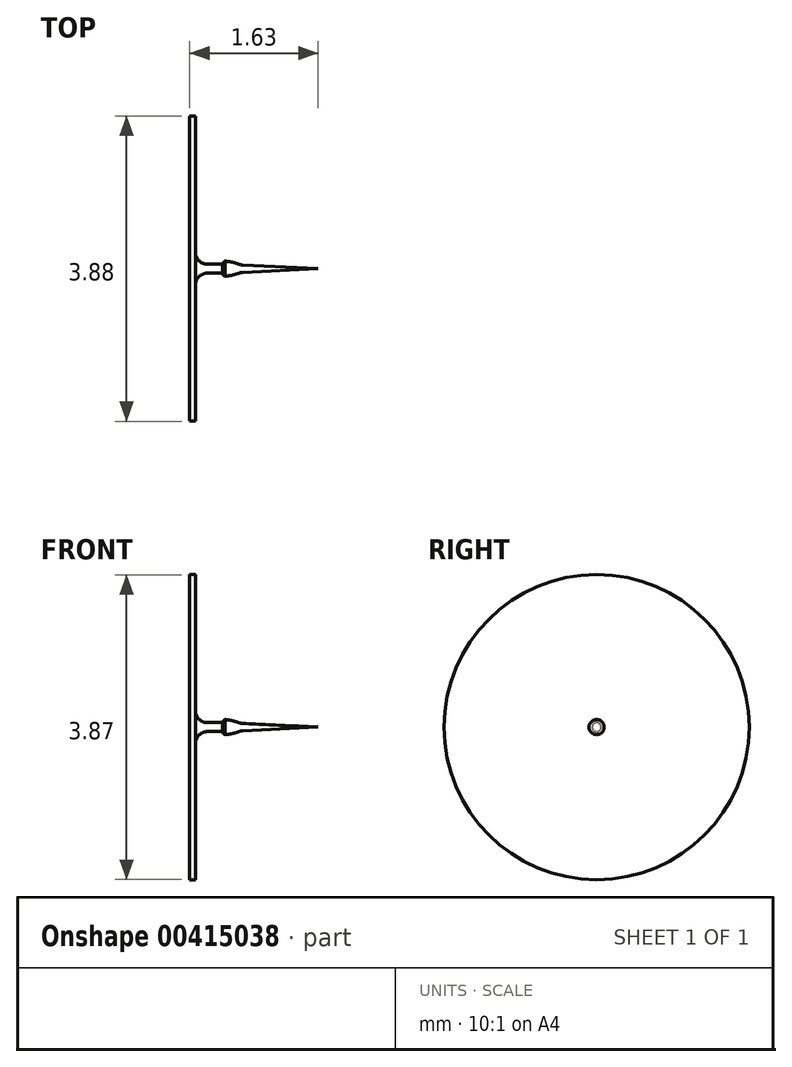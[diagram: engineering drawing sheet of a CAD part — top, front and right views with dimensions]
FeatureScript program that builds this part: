
annotation { "Feature Type Name" : "Feature", "Feature Type Description" : "" }
export const myFeature = defineFeature(function(context is Context, id is Id, definition is map)
    precondition{}
    {
        {
            var Q0;
            Q0=qCreatedBy(makeId("Front.planeOp"),FACE);
            var sketch = newSketch(context, id + "F0", { "sketchPlane" : qUnion([Q0])});
            skLineSegment(sketch, "E0.bottom", {"start": v(-10.35, 1.78) * mm, "end": v(14.65, 1.78) * mm});
            skLineSegment(sketch, "E0.top", {"start": v(-10.35, 0.78) * mm, "end": v(14.65, 0.78) * mm});
            skLineSegment(sketch, "E0.left", {"start": v(-10.35, 1.78) * mm, "end": v(-10.35, 0.78) * mm});
            skLineSegment(sketch, "E0.right", {"start": v(14.65, 1.78) * mm, "end": v(14.65, 0.78) * mm});
            skLineSegment(sketch, "E1", {"start": v(-10.35, -1.22) * mm, "end": v(14.65, -1.22) * mm});
            skLineSegment(sketch, "E2.bottom", {"start": v(8.36, 0.78) * mm, "end": v(8.11, 0.78) * mm});
            skLineSegment(sketch, "E2.top", {"start": v(8.36, 0.43) * mm, "end": v(8.11, 0.43) * mm});
            skLineSegment(sketch, "E2.left", {"start": v(8.36, 0.78) * mm, "end": v(8.36, 0.43) * mm});
            skLineSegment(sketch, "E2.right", {"start": v(8.11, 0.78) * mm, "end": v(8.11, 0.43) * mm});
            skArc(sketch, "E3", {"start": v(-10.35, 0.78) * mm, "mid": v(-9.78, 0.5) * mm, "end": v(-9.2, 0.78) * mm});
            skArc(sketch, "E4", {"start": v(5.04, 1.78) * mm, "mid": v(2.54, 2.32) * mm, "end": v(0.04, 1.78) * mm});
            skLineSegment(sketch, "E5.bottom", {"start": v(5.04, 0.71) * mm, "end": v(8.06, 0.71) * mm});
            skLineSegment(sketch, "E5.top", {"start": v(5.04, -0.04) * mm, "end": v(8.06, -0.04) * mm});
            skLineSegment(sketch, "E5.left", {"start": v(5.04, 0.71) * mm, "end": v(5.04, -0.04) * mm});
            skLineSegment(sketch, "E5.right", {"start": v(8.06, 0.71) * mm, "end": v(8.06, -0.06) * mm});
            skLineSegment(sketch, "E6.bottom", {"start": v(8.06, 0.35) * mm, "end": v(8.72, 0.35) * mm});
            skLineSegment(sketch, "E6.top", {"start": v(8.06, -1.22) * mm, "end": v(8.72, -1.22) * mm});
            skLineSegment(sketch, "E6.left", {"start": v(8.06, 0.35) * mm, "end": v(8.06, -1.22) * mm});
            skLineSegment(sketch, "E6.right", {"start": v(8.72, 0.35) * mm, "end": v(8.72, -1.22) * mm});
            skLineSegment(sketch, "E7.bottom", {"start": v(7.8, -0.04) * mm, "end": v(8.06, -0.04) * mm});
            skLineSegment(sketch, "E7.top", {"start": v(7.8, -1.22) * mm, "end": v(8.06, -1.22) * mm});
            skLineSegment(sketch, "E7.left", {"start": v(7.8, -0.04) * mm, "end": v(7.8, -1.22) * mm});
            skLineSegment(sketch, "E7.right", {"start": v(8.06, -0.04) * mm, "end": v(8.06, -1.22) * mm});
            skLineSegment(sketch, "E8.bottom", {"start": v(-3.72, 0.71) * mm, "end": v(-8.72, 0.71) * mm});
            skLineSegment(sketch, "E8.top", {"start": v(-3.72, -0.04) * mm, "end": v(-8.72, -0.04) * mm});
            skLineSegment(sketch, "E8.left", {"start": v(-3.72, 0.71) * mm, "end": v(-3.72, -0.04) * mm});
            skLineSegment(sketch, "E8.right", {"start": v(-8.72, 0.71) * mm, "end": v(-8.72, -0.04) * mm});
            skLineSegment(sketch, "E9.bottom", {"start": v(-8.72, -0.04) * mm, "end": v(-8.47, -0.04) * mm});
            skLineSegment(sketch, "E9.top", {"start": v(-8.72, -0.29) * mm, "end": v(-8.47, -0.29) * mm});
            skLineSegment(sketch, "E9.left", {"start": v(-8.72, -0.04) * mm, "end": v(-8.72, -0.29) * mm});
            skLineSegment(sketch, "E9.right", {"start": v(-8.47, -0.04) * mm, "end": v(-8.47, -0.29) * mm});
            skLineSegment(sketch, "E10.bottom", {"start": v(-8.72, -1.14) * mm, "end": v(-8.47, -1.14) * mm});
            skLineSegment(sketch, "E10.top", {"start": v(-8.72, -0.99) * mm, "end": v(-8.47, -0.99) * mm});
            skLineSegment(sketch, "E10.left", {"start": v(-8.72, -1.14) * mm, "end": v(-8.72, -0.99) * mm});
            skLineSegment(sketch, "E10.right", {"start": v(-8.47, -1.14) * mm, "end": v(-8.47, -0.99) * mm});
            skLineSegment(sketch, "E11.left", {"start": v(-8.72, -0.29) * mm, "end": v(-8.72, -0.99) * mm});
            skLineSegment(sketch, "E11.right", {"start": v(-8.47, -0.29) * mm, "end": v(-8.47, -0.99) * mm});
            skLineSegment(sketch, "E12", {"start": v(-8.86, -1.22) * mm, "end": v(-8.86, 0.71) * mm});
            skLineSegment(sketch, "E13", {"start": v(-8.86, 0.71) * mm, "end": v(-8.79, 0.71) * mm});
            skLineSegment(sketch, "E14", {"start": v(-8.79, 0.71) * mm, "end": v(-8.79, -1.17) * mm});
            skLineSegment(sketch, "E15", {"start": v(-8.79, -1.17) * mm, "end": v(-8.38, -1.17) * mm});
            skLineSegment(sketch, "E16", {"start": v(-8.38, -1.17) * mm, "end": v(-7.23, -1.22) * mm});
            skArc(sketch, "E17", {"start": v(-8.4, -1.13) * mm, "mid": v(-8.43, -1.14) * mm, "end": v(-8.44, -1.17) * mm});
            skArc(sketch, "E18", {"start": v(-8.21, -1.18) * mm, "mid": v(-8.3, -1.14) * mm, "end": v(-8.4, -1.13) * mm});
            skSolve(sketch);
        }
        {
            var Q0;
            {var subQ0=sQuery(id+"F0.wireOp",EDGE,"E12");Q0=makeQuery(id+"F0.imprint","IMPRINT",FACE,{"disambiguationData":[TD([[makeQuery(id+"F0.imprint","IMPRINT",EDGE,{"derivedFrom":subQ0}),-1.0]])]});}
            var Q1;
            {var subQ3=sQuery(id+"F0.wireOp",EDGE,"E17");Q1=makeQuery(id+"F0.imprint","IMPRINT",FACE,{"disambiguationData":[TD([[makeQuery(id+"F0.imprint","IMPRINT",EDGE,{"derivedFrom":subQ3}),1.0]])]});}
            var Q2;
            Q2=sQuery(id+"F0.wireOp",EDGE,"E1");
            revolve(context, id + "F1", {"entities" : qUnion([Q0, Q1]), "axis" : qUnion([Q2]), "revolveType" : RevolveType.FULL});
        }
        {
            var Q0;
            Q0=makeQuery(id+"F1.opRevolve","SWEPT_EDGE",EDGE,{"disambiguationData":[OSD([sQuery(id+"F0.wireOp",EDGE,"E14"),sQuery(id+"F0.wireOp",EDGE,"E15")])]});
            var Q1;
            Q1=makeQuery(id+"F1.opRevolve","SWEPT_EDGE",EDGE,{"disambiguationData":[OSD([sQuery(id+"F0.wireOp",EDGE,"E16"),sQuery(id+"F0.wireOp",EDGE,"E18")])]});
            fillet(context, id + "F2", {"entities" : qUnion([Q0, Q1]), "radius" : 0.15 * mm, "tangentPropagation" : true, "allowEdgeOverflow" : false});
        }
    });
